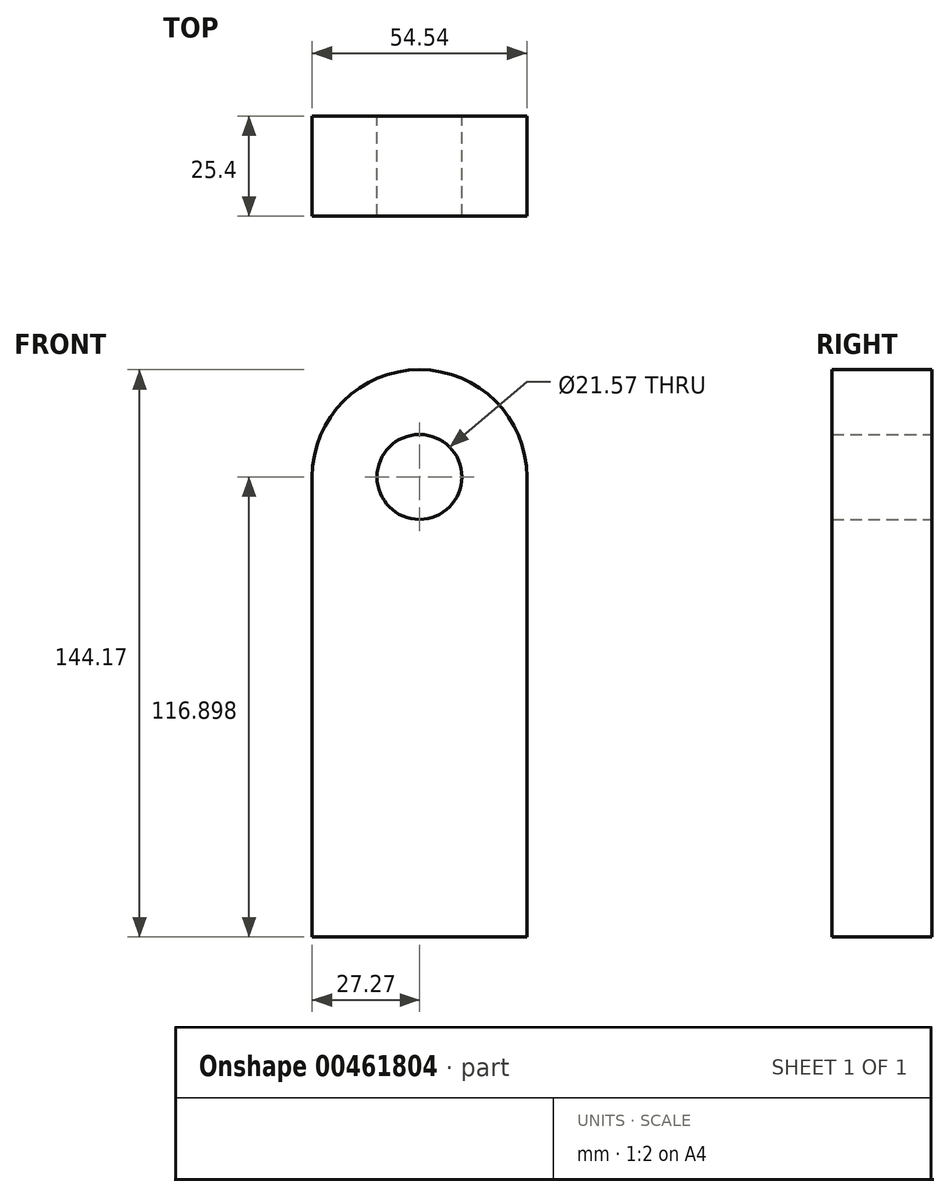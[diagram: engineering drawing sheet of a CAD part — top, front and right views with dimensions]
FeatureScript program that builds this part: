
annotation { "Feature Type Name" : "Feature", "Feature Type Description" : "" }
export const myFeature = defineFeature(function(context is Context, id is Id, definition is map)
    precondition{}
    {
        {
            var Q0;
            Q0=qCreatedBy(makeId("Front.planeOp"),FACE);
            var sketch = newSketch(context, id + "F0", { "sketchPlane" : qUnion([Q0])});
            skLineSegment(sketch, "E0.top", {"start": v(-27.27, -58.45) * mm, "end": v(27.27, -58.45) * mm});
            skLineSegment(sketch, "E0.left", {"start": v(-27.27, 58.45) * mm, "end": v(-27.27, -58.45) * mm});
            skLineSegment(sketch, "E0.right", {"start": v(27.27, 58.45) * mm, "end": v(27.27, -58.45) * mm});
            skPoint(sketch, "E0.middle", {"position": v(0, 0) * mm});
            skArc(sketch, "E1", {"start": v(27.27, 58.45) * mm, "mid": v(0, 85.72) * mm, "end": v(-27.27, 58.45) * mm});
            skArc(sketch, "E2", {"start": v(-10.78, 58.45) * mm, "mid": v(0, 69.23) * mm, "end": v(10.78, 58.45) * mm});
            skArc(sketch, "E3", {"start": v(10.78, 58.45) * mm, "mid": v(0, 47.66) * mm, "end": v(-10.78, 58.45) * mm});
            skSolve(sketch);
        }
        {
            var Q0;
            Q0=makeQuery(id+"F0.imprint","IMPRINT",FACE,{"disambiguationData":[TD([[makeQuery(id+"F0.imprint","IMPRINT",EDGE,{"derivedFrom":sQuery(id+"F0.wireOp",EDGE,"E0.top")}),1.0]])]});
            extrude(context, id + "F1", {"entities" : qUnion([Q0]), "depth" : 25.4 * mm});
        }
    });
